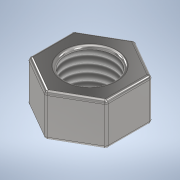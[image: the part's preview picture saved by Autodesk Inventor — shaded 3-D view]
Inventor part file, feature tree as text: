
AUTODESK INVENTOR PART (.ipt)
format: ipt  version: 2021 (Build 250183000, 183)  size: 163,840 bytes
history: native  units: mm
features: extrude x1, fillet x1, thread x1, sketch x1
ambient origin geometry x8: Origin, YZ Plane, XZ Plane, XY Plane, X Axis, Y Axis, Z Axis, Center Point
bodies: Body1 (feature_tree)
feature tree (4):
  extrude  "Extrusion3"  Depth=13.0mm
  fillet  "Fillet2"  Radius=7.0mm
  thread  "Thread2"  [1 undecoded]
  sketch  "Sketch1"  dims[d0=8.0mm d9=13.0mm d10=7.0mm d11=0.0mm d12=0.5mm d13=6.0mm d14=0.0mm]
note: 1 required parameter value undecoded (feature->parameter linkage not recoverable at this tier; creation-order binding heuristic only, values carry confidence <= 0.55)
